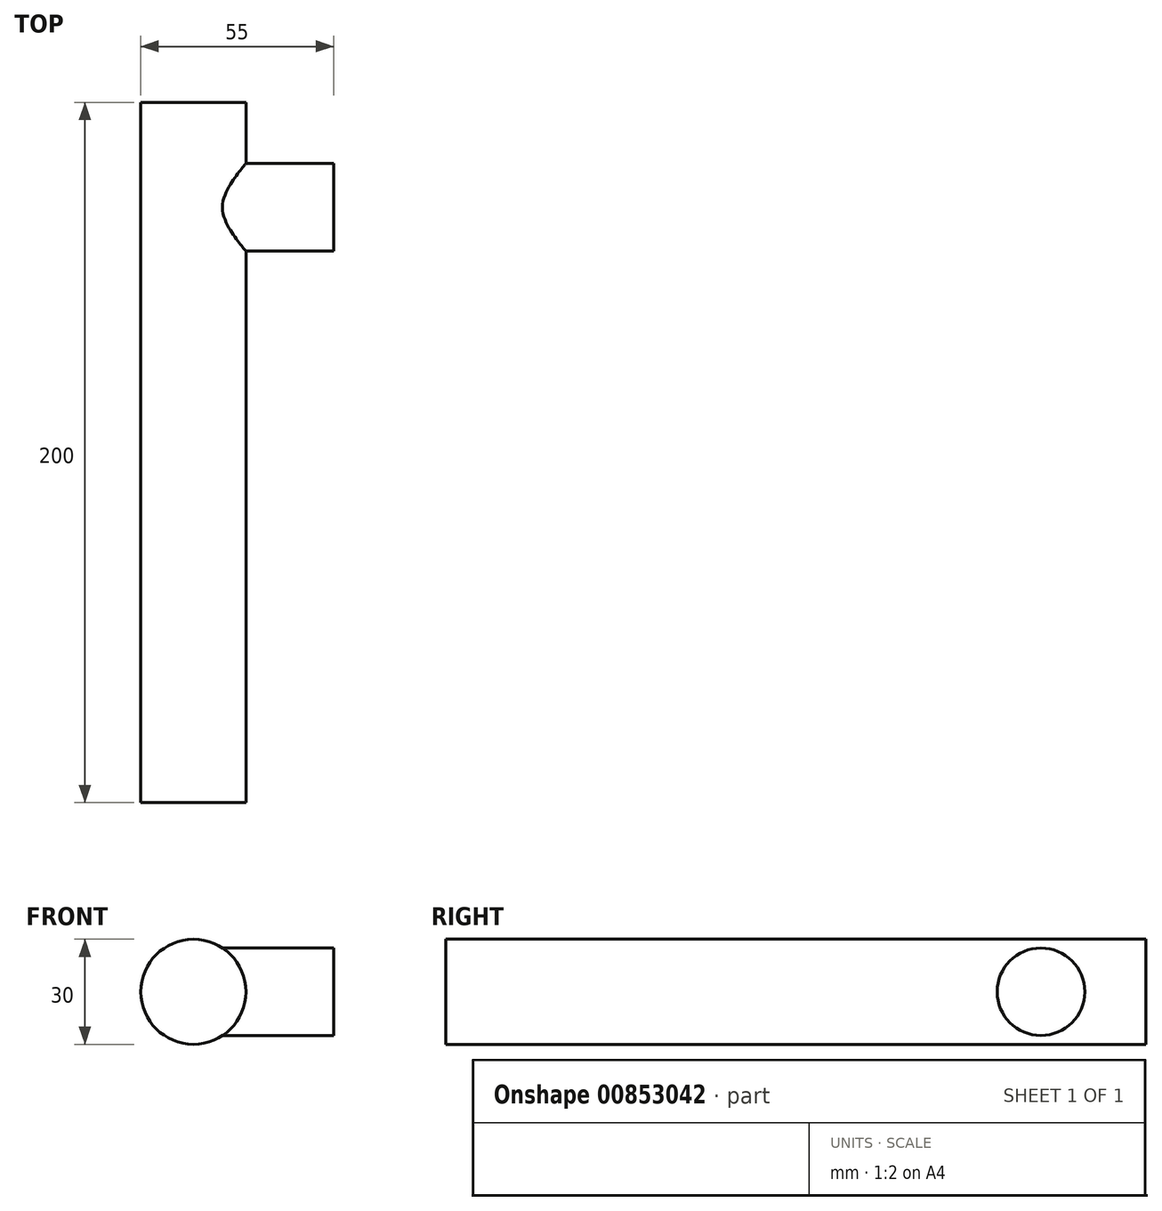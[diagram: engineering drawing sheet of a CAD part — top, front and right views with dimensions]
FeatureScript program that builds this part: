
annotation { "Feature Type Name" : "Feature", "Feature Type Description" : "" }
export const myFeature = defineFeature(function(context is Context, id is Id, definition is map)
    precondition{}
    {
        {
            var Q0;
            Q0=qCreatedBy(makeId("Front.planeOp"),FACE);
            var sketch = newSketch(context, id + "F0", { "sketchPlane" : qUnion([Q0])});
            skCircle(sketch, "E0", {"center": v(0, 0) * mm, "radius": 15 * mm});
            skSolve(sketch);
        }
        {
            var Q0;
            Q0=makeQuery(id+"F0.imprint","IMPRINT",FACE,{"disambiguationData":[TD([[makeQuery(id+"F0.imprint","IMPRINT",EDGE,{"derivedFrom":sQuery(id+"F0.wireOp",EDGE,"E0")}),1.0]])]});
            extrude(context, id + "F1", {"entities" : qUnion([Q0]), "depth" : 200 * mm, "offsetDistance" : 25 * mm});
        }
        {
            var Q0;
            Q0=qCreatedBy(makeId("Right.planeOp"),FACE);
            var sketch = newSketch(context, id + "F2", { "sketchPlane" : qUnion([Q0])});
            skCircle(sketch, "E1", {"center": v(-30, 0) * mm, "radius": 12.5 * mm});
            skSolve(sketch);
        }
        {
            var Q0;
            Q0 = qSketchRegion(id + "F2", true);
            extrude(context, id + "F3", {"entities" : qUnion([Q0]), "operationType" : NewBodyOperationType.ADD, "depth" : 40 * mm, "offsetDistance" : 25 * mm});
        }
    });
